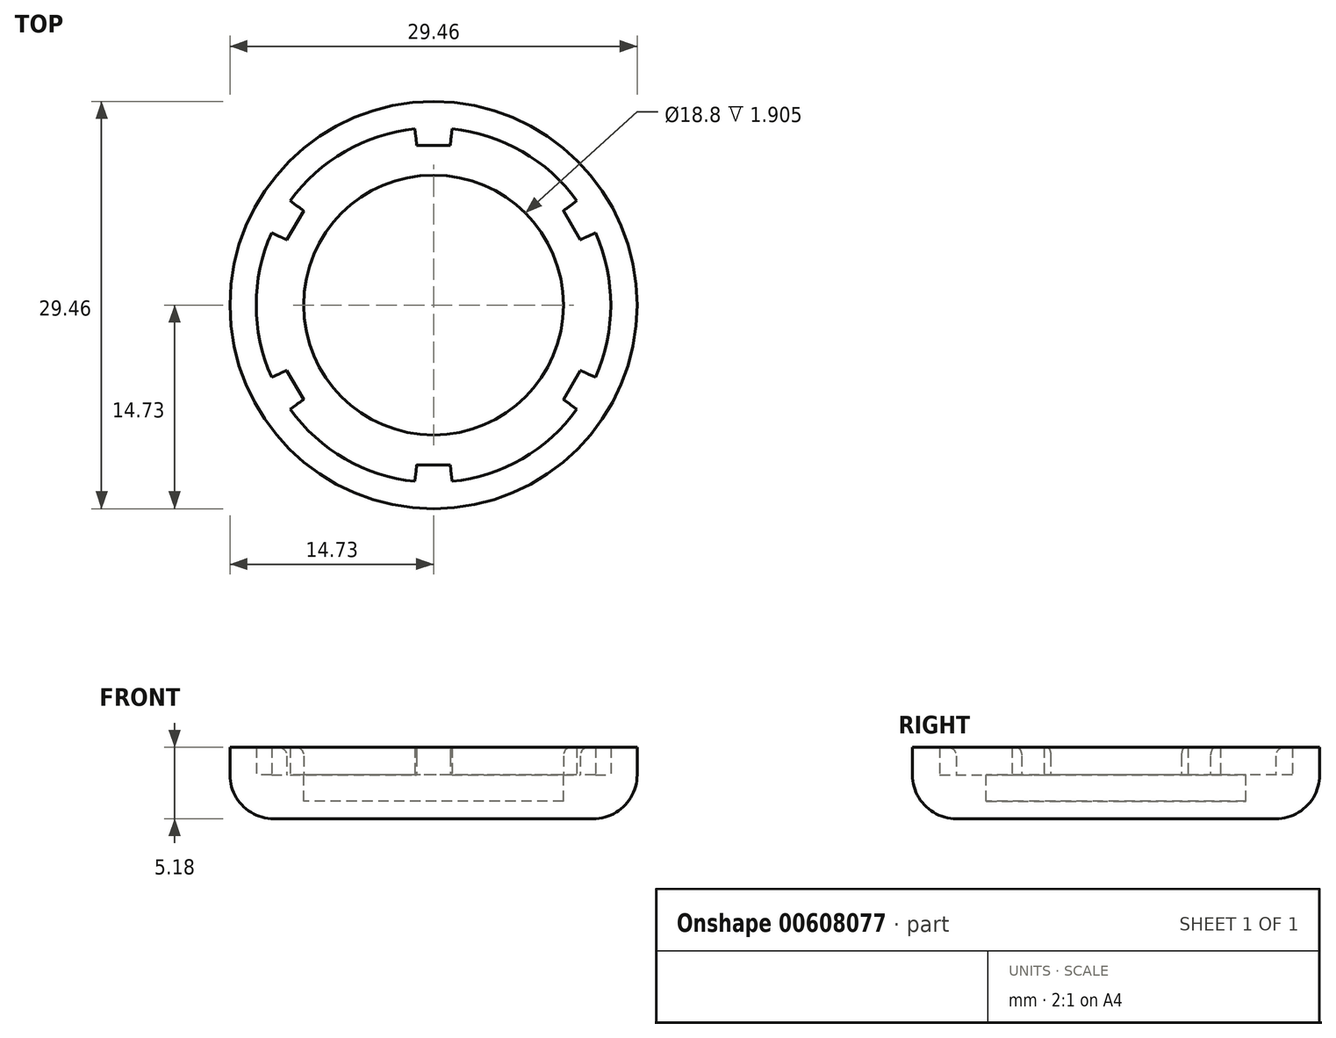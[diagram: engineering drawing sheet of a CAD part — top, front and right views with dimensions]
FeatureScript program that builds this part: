
annotation { "Feature Type Name" : "Feature", "Feature Type Description" : "" }
export const myFeature = defineFeature(function(context is Context, id is Id, definition is map)
    precondition{}
    {
        {
            var Q0;
            Q0=qCreatedBy(makeId("Top.planeOp"),FACE);
            var sketch = newSketch(context, id + "F0", { "sketchPlane" : qUnion([Q0])});
            skCircle(sketch, "E0", {"center": v(0, 0) * mm, "radius": 11.56 * mm, "construction": true});
            skArc(sketch, "E1", {"start": v(-1.34, 12.76) * mm, "mid": v(-6.41, 11.1) * mm, "end": v(-10.38, 7.54) * mm});
            skLineSegment(sketch, "E2", {"start": v(0, 12.83) * mm, "end": v(0, 11.56) * mm, "construction": true});
            skLineSegment(sketch, "E3", {"start": v(-1.34, 12.76) * mm, "end": v(-1.21, 11.56) * mm});
            skLineSegment(sketch, "E4.MirrorCS", {"start": v(1.34, 12.76) * mm, "end": v(1.21, 11.56) * mm});
            skLineSegment(sketch, "E5", {"start": v(-1.21, 11.56) * mm, "end": v(1.21, 11.56) * mm});
            skCircle(sketch, "E6", {"center": v(0, 0) * mm, "radius": 14.73 * mm});
            skLineSegment(sketch, "E7.1.0", {"start": v(-10.38, 7.54) * mm, "end": v(-9.4, 6.83) * mm});
            skLineSegment(sketch, "E7.1.1", {"start": v(-10.62, 4.73) * mm, "end": v(-9.4, 6.83) * mm});
            skLineSegment(sketch, "E7.1.2", {"start": v(-11.72, 5.22) * mm, "end": v(-10.62, 4.73) * mm});
            skLineSegment(sketch, "E7.2.0", {"start": v(-11.72, -5.22) * mm, "end": v(-10.62, -4.73) * mm});
            skLineSegment(sketch, "E7.2.1", {"start": v(-9.4, -6.83) * mm, "end": v(-10.62, -4.73) * mm});
            skLineSegment(sketch, "E7.2.2", {"start": v(-10.38, -7.54) * mm, "end": v(-9.4, -6.83) * mm});
            skLineSegment(sketch, "E7.3.0", {"start": v(-1.34, -12.76) * mm, "end": v(-1.21, -11.56) * mm});
            skLineSegment(sketch, "E7.3.1", {"start": v(1.21, -11.56) * mm, "end": v(-1.21, -11.56) * mm});
            skLineSegment(sketch, "E7.3.2", {"start": v(1.34, -12.76) * mm, "end": v(1.21, -11.56) * mm});
            skLineSegment(sketch, "E7.4.0", {"start": v(10.38, -7.54) * mm, "end": v(9.4, -6.83) * mm});
            skLineSegment(sketch, "E7.4.1", {"start": v(10.62, -4.73) * mm, "end": v(9.4, -6.83) * mm});
            skLineSegment(sketch, "E7.4.2", {"start": v(11.72, -5.22) * mm, "end": v(10.62, -4.73) * mm});
            skLineSegment(sketch, "E7.5.0", {"start": v(11.72, 5.22) * mm, "end": v(10.62, 4.73) * mm});
            skLineSegment(sketch, "E7.5.1", {"start": v(9.4, 6.83) * mm, "end": v(10.62, 4.73) * mm});
            skLineSegment(sketch, "E7.5.2", {"start": v(10.38, 7.54) * mm, "end": v(9.4, 6.83) * mm});
            skArc(sketch, "E8.trimOffspring", {"start": v(10.38, 7.54) * mm, "mid": v(6.41, 11.1) * mm, "end": v(1.34, 12.76) * mm});
            skArc(sketch, "E9.trimOffspring", {"start": v(11.72, -5.22) * mm, "mid": v(12.83, 0) * mm, "end": v(11.72, 5.22) * mm});
            skArc(sketch, "E10.trimOffspring", {"start": v(1.34, -12.76) * mm, "mid": v(6.41, -11.1) * mm, "end": v(10.38, -7.54) * mm});
            skArc(sketch, "E11.trimOffspring", {"start": v(-10.38, -7.54) * mm, "mid": v(-6.41, -11.1) * mm, "end": v(-1.34, -12.76) * mm});
            skArc(sketch, "E12.trimOffspring", {"start": v(-11.72, 5.22) * mm, "mid": v(-12.83, 0) * mm, "end": v(-11.72, -5.22) * mm});
            skSolve(sketch);
        }
        {
            var Q0;
            Q0=makeQuery(id+"F0.imprint","IMPRINT",FACE,{"disambiguationData":[TD([[makeQuery(id+"F0.imprint","IMPRINT",EDGE,{"derivedFrom":sQuery(id+"F0.wireOp",EDGE,"E1")}),1.0]])]});
            var Q1;
            Q1=makeQuery(id+"F0.imprint","IMPRINT",FACE,{"disambiguationData":[TD([[makeQuery(id+"F0.imprint","IMPRINT",EDGE,{"derivedFrom":sQuery(id+"F0.wireOp",EDGE,"E1")}),-1.0]])]});
            extrude(context, id + "F1", {"entities" : qUnion([Q0, Q1]), "oppositeDirection" : true, "depth" : 3.17 * mm, "offsetDistance" : 25.4 * mm});
        }
        {
            var Q0;
            Q0 = qSketchRegion(id + "F0", true);
            extrude(context, id + "F2", {"entities" : qUnion([Q0]), "operationType" : NewBodyOperationType.ADD, "depth" : 2 * mm, "offsetDistance" : 25.4 * mm});
        }
        {
            var Q0;
            Q0=makeQuery(id+"F1.opExtrude","CAP_FACE",FACE,{"disambiguationData":[OSD([sQuery(id+"F0.wireOp",EDGE,"E6")])],"isStart":true});
            var sketch = newSketch(context, id + "F3", { "sketchPlane" : qUnion([Q0])});
            skCircle(sketch, "E13", {"center": v(0, 0) * mm, "radius": 9.4 * mm});
            skSolve(sketch);
        }
        {
            var Q0;
            Q0=makeQuery(id+"F3.imprint","IMPRINT",FACE,{"disambiguationData":[TD([[makeQuery(id+"F3.imprint","IMPRINT",EDGE,{"derivedFrom":sQuery(id+"F3.wireOp",EDGE,"E13")}),1.0]])]});
            extrude(context, id + "F4", {"entities" : qUnion([Q0]), "operationType" : NewBodyOperationType.REMOVE, "oppositeDirection" : true, "depth" : 1.9 * mm, "offsetDistance" : 25.4 * mm});
        }
        {
            var Q0;
            Q0=makeQuery(id+"F1.opExtrude","CAP_EDGE",EDGE,{"disambiguationData":[OSD([sQuery(id+"F0.wireOp",EDGE,"E6")])],"isStart":false});
            fillet(context, id + "F5", {"entities" : qUnion([Q0]), "radius" : 3.17 * mm, "tangentPropagation" : true, "allowEdgeOverflow" : false});
        }
        {
            var Q0;
            Q0=makeQuery(id+"F2.opExtrude","CAP_EDGE",EDGE,{"disambiguationData":[OSD([sQuery(id+"F0.wireOp",EDGE,"E5")])],"isStart":false});
            var Q1;
            Q1=makeQuery(id+"F2.opExtrude","CAP_EDGE",EDGE,{"disambiguationData":[OSD([sQuery(id+"F0.wireOp",EDGE,"E7.4.1")])],"isStart":false});
            var Q2;
            Q2=makeQuery(id+"F2.opExtrude","CAP_EDGE",EDGE,{"disambiguationData":[OSD([sQuery(id+"F0.wireOp",EDGE,"E7.1.1")])],"isStart":false});
            var Q3;
            Q3=makeQuery(id+"F2.opExtrude","CAP_EDGE",EDGE,{"disambiguationData":[OSD([sQuery(id+"F0.wireOp",EDGE,"E7.2.1")])],"isStart":false});
            var Q4;
            Q4=makeQuery(id+"F2.opExtrude","CAP_EDGE",EDGE,{"disambiguationData":[OSD([sQuery(id+"F0.wireOp",EDGE,"E7.3.1")])],"isStart":false});
            var Q5;
            Q5=makeQuery(id+"F2.opExtrude","CAP_EDGE",EDGE,{"disambiguationData":[OSD([sQuery(id+"F0.wireOp",EDGE,"E7.5.1")])],"isStart":false});
            fillet(context, id + "F6", {"entities" : qUnion([Q0, Q1, Q2, Q3, Q4, Q5]), "radius" : 0.64 * mm, "tangentPropagation" : true, "allowEdgeOverflow" : false});
        }
    });
